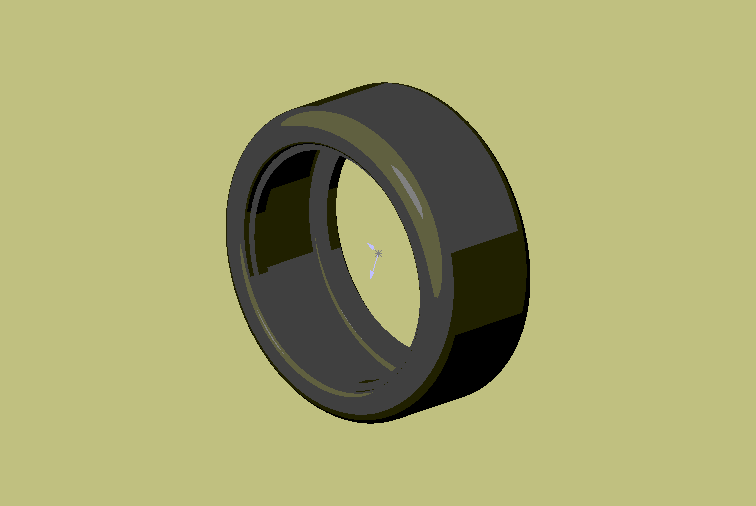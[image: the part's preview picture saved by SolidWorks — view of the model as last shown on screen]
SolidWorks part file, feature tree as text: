
SOLIDWORKS PART (.sldprt)
format: sldprt  version: not decoded by parser v0  size: 271,360 bytes
history: native  units: mm
features: plane x3, sketch x2, mirror x2, material x1, extrude x1, fillet x1, cut_extrude x1, shell x1 (+8 scaffold rows collapsed)
feature tree (20):
  scaffold x8  (default folders/planes/origin — collapsed)
  material  "Matériau <non spécifié>"
  plane  "Plane1"
  plane  "Plane2"
  plane  "Plane3"
  sketch  "Esquisse1"  dims[D1=47.0mm D2=64.0mm]
  extrude  "Base-Extrusion"  Depth=26mm
  fillet  "Congé1"  Radius=4mm
  sketch  "Esquisse2"  dims[D1=50.0mm]
  cut_extrude  "Enlèv. mat.-Extru.1"  Depth=2mm
  mirror  "Symétrie1"
  mirror  "Congé2"
  shell  "Coque1"  Thickness=2.5mm
decode coverage: 6 of 8 modeling features carry decoded parameters
note: suppression state not decoded; provenance and decode notes live in map.json
